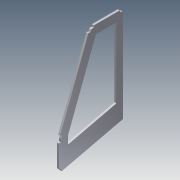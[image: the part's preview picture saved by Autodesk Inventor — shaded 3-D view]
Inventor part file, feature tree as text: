
AUTODESK INVENTOR PART (.ipt)
format: ipt  version: 2014 (Build 180170000, 170)  size: 188,416 bytes
history: native  units: mm
features: extrude x7, sketch x7, fillet x3
ambient origin geometry x8: Origin, YZ Plane, XZ Plane, XY Plane, X Axis, Y Axis, Z Axis, Center Point
bodies: Solid1 (feature_tree)
feature tree (17):
  extrude  "Extrusion1"  Depth=186.0mm
  extrude  "Extrusion2"  Depth=95.0mm
  extrude  "Extrusion3"  Depth=6.0mm
  extrude  "Extrusion6"  Depth=6.0mm
  fillet  "Fillet2"  Radius=8.1mm
  fillet  "Fillet3"  Radius=8.1mm
  extrude  "Extrusion4"  Depth=3.0mm
  extrude  "Extrusion7"  Depth=20.0mm
  extrude  "Extrusion8"  Depth=20.0mm
  fillet  "Fillet4"  Radius=4.0mm
  sketch  "Sketch1"  dims[d0=325.0mm d1=186.0mm]
  sketch  "Sketch2"  dims[d2=85.0mm d3=95.0mm]
  sketch  "Sketch3"  dims[d4=6.0mm d5=0.0mm d6=6.0mm]
  sketch  "Sketch4"  dims[d9=6.0mm d10=0.0mm d12=6.0mm d13=8.1mm d17=8.1mm]
  sketch  "Sketch6"  dims[d20=6.0mm d21=0.0mm d22=3.0mm]
  sketch  "Sketch7"  dims[d23=2.0mm d24=20.0mm]
  sketch  "Sketch8"  dims[d26=20.0mm d27=20.0mm d29=4.0mm d30=0.0mm d33=240.0mm d34=91.0mm d35=6.0mm d36=8.1mm d38=50.0mm d39=25.0mm d40=10.0mm d41=0.0mm d42=10.0mm d43=0.0mm d44=10.0mm d45=6.0mm d46=0.0mm d47=8.1mm d48=8.1mm d49=2.0mm]
